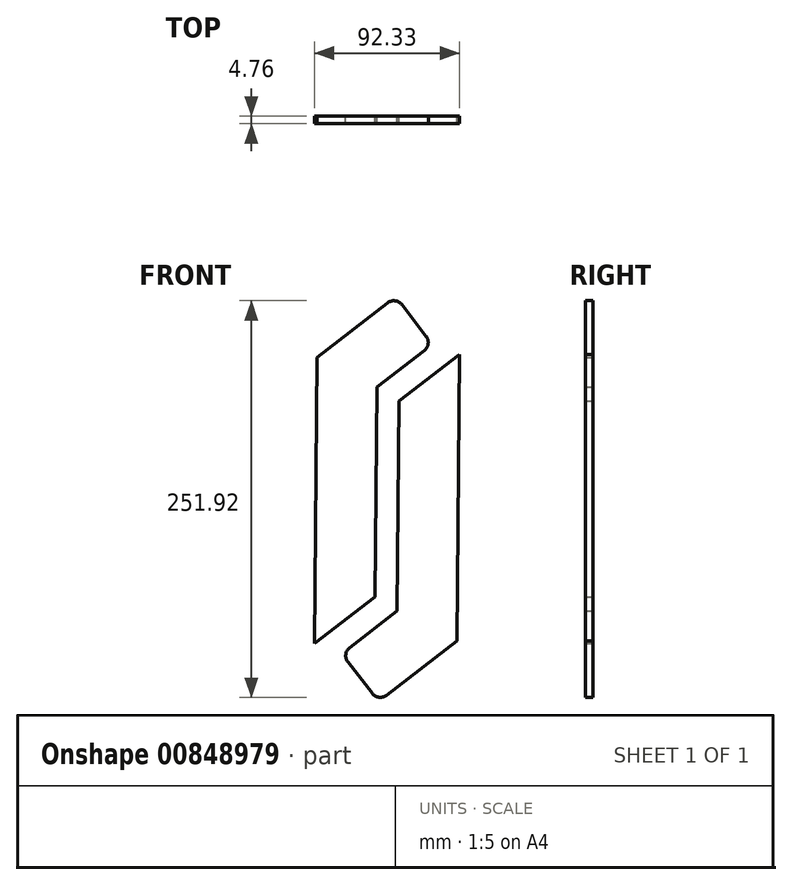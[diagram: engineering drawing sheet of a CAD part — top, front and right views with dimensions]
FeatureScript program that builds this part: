
annotation { "Feature Type Name" : "Feature", "Feature Type Description" : "" }
export const myFeature = defineFeature(function(context is Context, id is Id, definition is map)
    precondition{}
    {
        {
            var Q0;
            Q0=qCreatedBy(makeId("Front.planeOp"),FACE);
            var sketch = newSketch(context, id + "F0", { "sketchPlane" : qUnion([Q0])});
            skArc(sketch, "E0.MirrorCS", {"start": v(-87.4, 5.3) * mm, "mid": v(-89.82, 1.09) * mm, "end": v(-88.55, -3.6) * mm});
            skArc(sketch, "E1.MirrorCS", {"start": v(-73.03, -23.7) * mm, "mid": v(-68.82, -26.13) * mm, "end": v(-64.12, -24.86) * mm});
            skPoint(sketch, "E2.MirrorP", {"position": v(-57.25, 28.59) * mm});
            skLineSegment(sketch, "E3.MirrorCS", {"start": v(-55.9, 161.93) * mm, "end": v(-17.5, 191.57) * mm});
            skLineSegment(sketch, "E4.MirrorCS", {"start": v(-55.9, 161.93) * mm, "end": v(-57.25, 28.59) * mm});
            skLineSegment(sketch, "E5.MirrorCS", {"start": v(-87.4, 5.3) * mm, "end": v(-57.25, 28.59) * mm});
            skLineSegment(sketch, "E6.MirrorCS", {"start": v(-64.12, -24.86) * mm, "end": v(-19.34, 9.72) * mm});
            skLineSegment(sketch, "E7.MirrorCS", {"start": v(-73.03, -23.7) * mm, "end": v(-88.55, -3.6) * mm});
            skLineSegment(sketch, "E8.0", {"start": v(-17.5, 191.57) * mm, "end": v(-19.34, 9.72) * mm});
            skArc(sketch, "E9.MirrorCS", {"start": v(-54.3, 223.27) * mm, "mid": v(-58.5, 225.68) * mm, "end": v(-63.2, 224.41) * mm});
            skArc(sketch, "E10.MirrorCS", {"start": v(-39.92, 194.25) * mm, "mid": v(-37.5, 198.47) * mm, "end": v(-38.77, 203.16) * mm});
            skPoint(sketch, "E11.MirrorP", {"position": v(-70.08, 170.97) * mm});
            skLineSegment(sketch, "E12.MirrorCS", {"start": v(-63.2, 224.41) * mm, "end": v(-107.99, 189.84) * mm});
            skLineSegment(sketch, "E13.MirrorCS", {"start": v(-109.83, 7.98) * mm, "end": v(-107.99, 189.84) * mm});
            skLineSegment(sketch, "E14.MirrorCS", {"start": v(-71.43, 37.63) * mm, "end": v(-109.83, 7.98) * mm});
            skLineSegment(sketch, "E15.MirrorCS", {"start": v(-54.3, 223.27) * mm, "end": v(-38.77, 203.16) * mm});
            skLineSegment(sketch, "E16.MirrorCS", {"start": v(-39.92, 194.25) * mm, "end": v(-70.08, 170.97) * mm});
            skLineSegment(sketch, "E17.MirrorCS", {"start": v(-71.43, 37.63) * mm, "end": v(-70.08, 170.97) * mm});
            skSolve(sketch);
        }
        {
            var Q0;
            Q0 = qSketchRegion(id + "F0", true);
            extrude(context, id + "F1", {"entities" : qUnion([Q0]), "depth" : 4.76 * mm, "offsetDistance" : 25.4 * mm});
        }
    });
